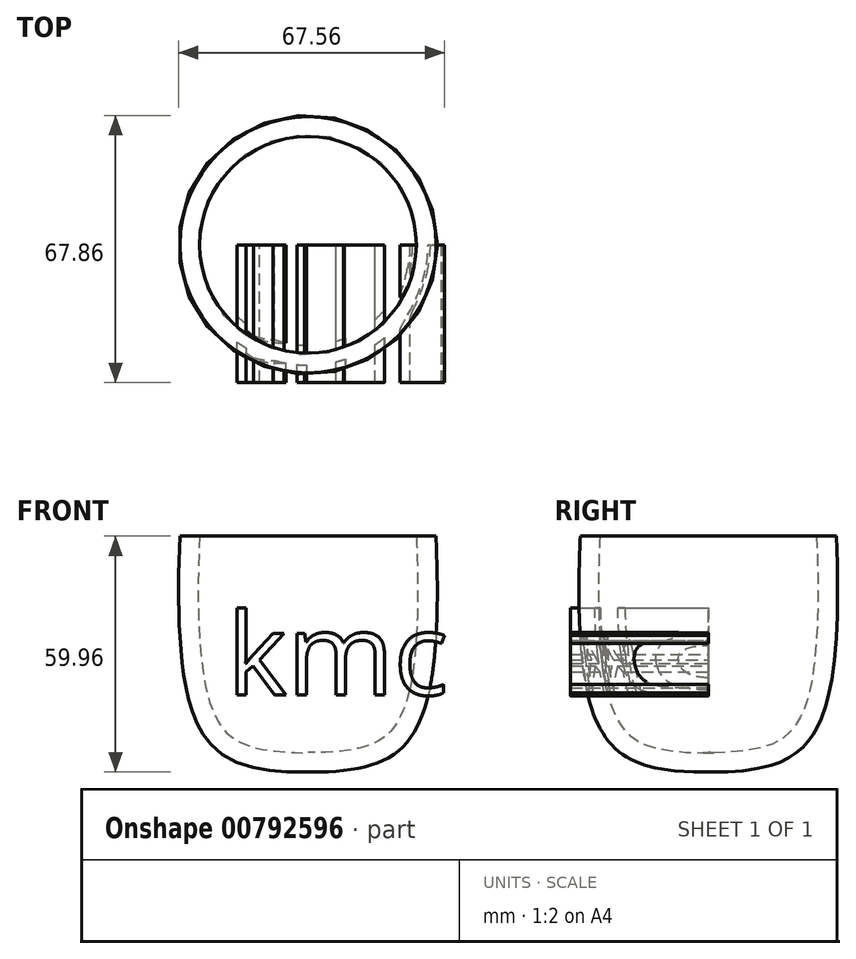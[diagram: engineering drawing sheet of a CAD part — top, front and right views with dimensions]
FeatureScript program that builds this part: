
annotation { "Feature Type Name" : "Feature", "Feature Type Description" : "" }
export const myFeature = defineFeature(function(context is Context, id is Id, definition is map)
    precondition{}
    {
        {
            var Q0;
            Q0=qCreatedBy(makeId("Front.planeOp"),FACE);
            var sketch = newSketch(context, id + "F0", { "sketchPlane" : qUnion([Q0])});
            skFitSpline(sketch, "E0", {"points": [v(32.25, 41.47) * mm, v(32.25, 5.92) * mm, v(22.16, -19.97) * mm, v(-15.14, -23.91) * mm], "startDerivative": vector(4.62, -103.8) * mm, "endDerivative": vector(-124.09, 8.63) * mm});
            skFitSpline(sketch, "E1.0", {"points": [v(27.26, 41.24) * mm, v(27.35, 39.08) * mm, v(27.54, 34.77) * mm, v(27.77, 28.36) * mm, v(27.89, 22) * mm, v(27.84, 16.73) * mm, v(27.7, 12.56) * mm, v(27.52, 9.44) * mm, v(27.28, 6.34) * mm, v(26.86, 2.24) * mm, v(26.1, -2.67) * mm, v(24.94, -7.04) * mm, v(23.73, -10.05) * mm, v(22.69, -12.04) * mm, v(21.71, -13.46) * mm, v(20.87, -14.44) * mm, v(20.2, -15.11) * mm, v(19.5, -15.72) * mm, v(18.51, -16.44) * mm, v(17.06, -17.25) * mm, v(14.98, -18.08) * mm, v(12.55, -18.73) * mm, v(9.82, -19.21) * mm, v(5.82, -19.63) * mm, v(0.24, -19.76) * mm, v(-7.08, -19.46) * mm, v(-12.2, -19.1) * mm, v(-14.8, -18.93) * mm]});
            skLineSegment(sketch, "E2", {"start": v(0, 35.32) * mm, "end": v(0, -45.85) * mm});
            skLineSegment(sketch, "E3", {"start": v(27.52, 35.27) * mm, "end": v(32.52, 35.27) * mm});
            skSolve(sketch);
        }
        {
            var Q0;
            {var subQ0=sQuery(id+"F0.wireOp",EDGE,"E0");Q0=makeQuery(id+"F0.imprint","IMPRINT",FACE,{"disambiguationData":[TD([[makeQuery(id+"F0.imprint","IMPRINT",EDGE,{"derivedFrom":subQ0}),-1.0]])]});}
            var Q1;
            Q1=sQuery(id+"F0.wireOp",EDGE,"E2");
            revolve(context, id + "F1", {"surfaceOperationType" : NewSurfaceOperationType.NEW, "entities" : qUnion([Q0]), "axis" : qUnion([Q1]), "revolveType" : RevolveType.FULL});
        }
        {
            var Q0;
            Q0=qCreatedBy(makeId("Front.planeOp"),FACE);
            var sketch = newSketch(context, id + "F2", { "sketchPlane" : qUnion([Q0])});
            skText(sketch, "E4", { "text": "kmc", "fontName": "OpenSans-Regular.ttf"});
            const initialGuessF2  = {"E4": [-0.02055, -0.00509, 1, 0, 0.02096]};
            skSetInitialGuess(sketch, initialGuessF2);
            skSolve(sketch);
        }
        {
            var Q0;
            Q0 = qSketchRegion(id + "F2", true);
            extrude(context, id + "F3", {"entities" : qUnion([Q0]), "operationType" : NewBodyOperationType.ADD, "depth" : 35 * mm, "offsetDistance" : 25 * mm});
        }
    });
